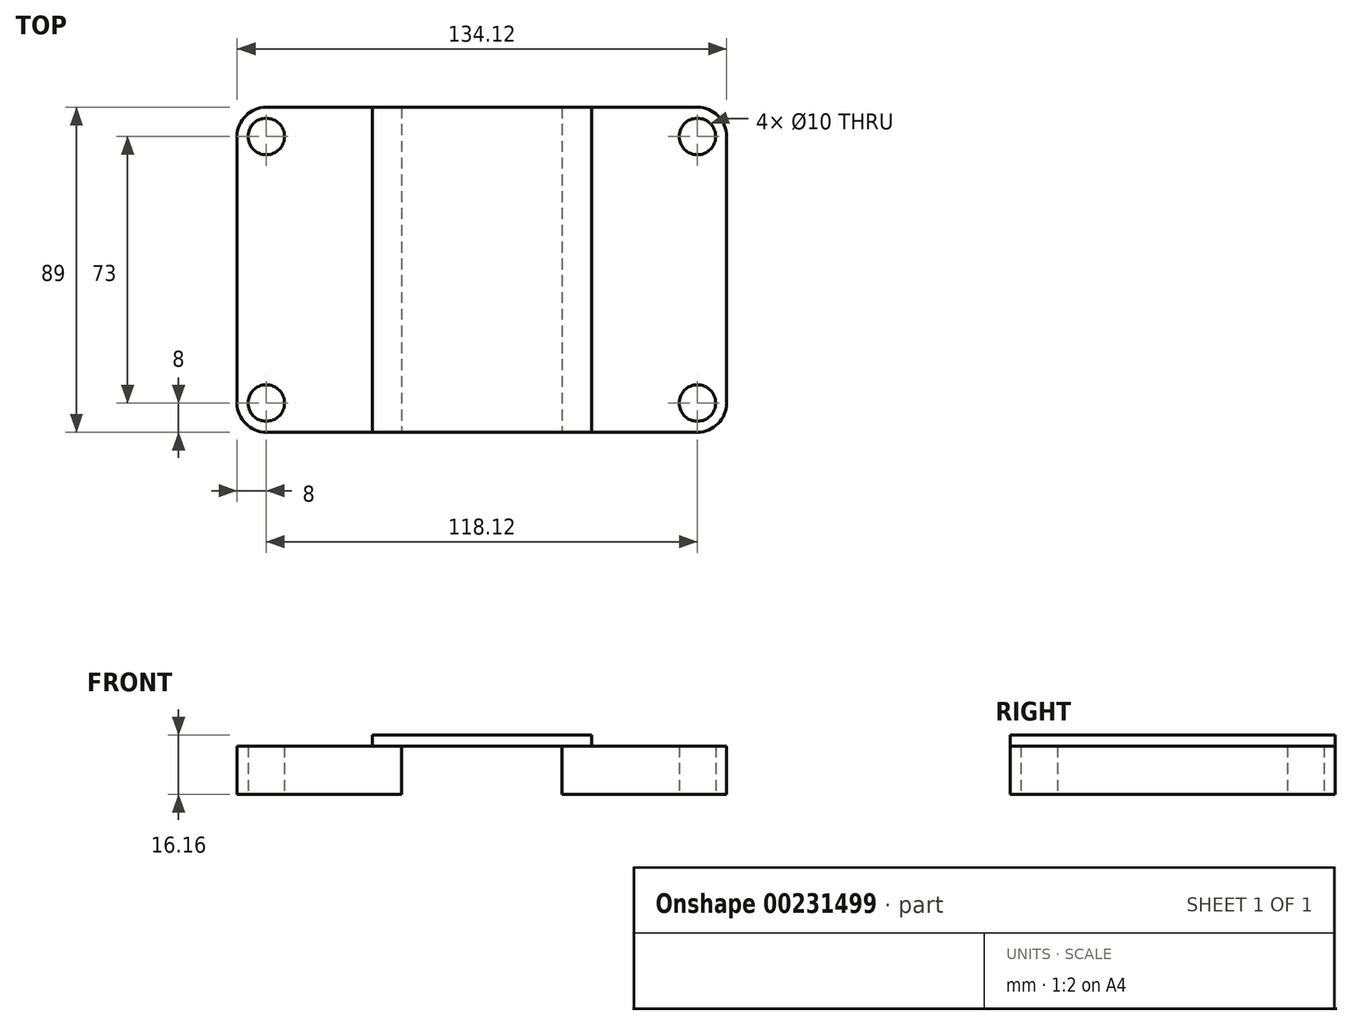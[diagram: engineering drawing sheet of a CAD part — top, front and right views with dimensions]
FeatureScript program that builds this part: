
annotation { "Feature Type Name" : "Feature", "Feature Type Description" : "" }
export const myFeature = defineFeature(function(context is Context, id is Id, definition is map)
    precondition{}
    {
        {
            var Q0;
            Q0=qCreatedBy(makeId("Top.planeOp"),FACE);
            var sketch = newSketch(context, id + "F0", { "sketchPlane" : qUnion([Q0])});
            skLineSegment(sketch, "E0.bottom", {"start": v(59.06, -44.5) * mm, "end": v(-59.06, -44.5) * mm});
            skLineSegment(sketch, "E0.top", {"start": v(67.06, 44.5) * mm, "end": v(-67.06, 44.5) * mm});
            skLineSegment(sketch, "E0.left", {"start": v(67.06, -36.5) * mm, "end": v(67.06, 36.5) * mm});
            skLineSegment(sketch, "E0.right", {"start": v(-67.06, -36.5) * mm, "end": v(-67.06, 36.5) * mm});
            skPoint(sketch, "E0.middle", {"position": v(0, 0) * mm});
            skLineSegment(sketch, "E1", {"start": v(-59.06, 44.5) * mm, "end": v(-21.96, 44.5) * mm});
            skLineSegment(sketch, "E2", {"start": v(-21.96, 44.5) * mm, "end": v(-21.96, -44.5) * mm});
            skLineSegment(sketch, "E3", {"start": v(-21.96, 44.5) * mm, "end": v(21.94, 44.5) * mm});
            skLineSegment(sketch, "E4", {"start": v(21.94, 44.5) * mm, "end": v(59.06, 44.5) * mm});
            skLineSegment(sketch, "E5", {"start": v(21.94, 44.5) * mm, "end": v(21.94, -44.5) * mm});
            skPoint(sketch, "E6.visualSharp", {"position": v(-67.06, 44.5) * mm});
            skArc(sketch, "E6.filletArc", {"start": v(-59.06, 44.5) * mm, "mid": v(-64.72, 42.16) * mm, "end": v(-67.06, 36.5) * mm});
            skPoint(sketch, "E7.visualSharp", {"position": v(67.06, 44.5) * mm});
            skArc(sketch, "E7.filletArc", {"start": v(67.06, 36.5) * mm, "mid": v(64.72, 42.16) * mm, "end": v(59.06, 44.5) * mm});
            skPoint(sketch, "E8.visualSharp", {"position": v(67.06, -44.5) * mm});
            skArc(sketch, "E8.filletArc", {"start": v(59.06, -44.5) * mm, "mid": v(64.72, -42.16) * mm, "end": v(67.06, -36.5) * mm});
            skPoint(sketch, "E9.visualSharp", {"position": v(-67.06, -44.5) * mm});
            skArc(sketch, "E9.filletArc", {"start": v(-67.06, -36.5) * mm, "mid": v(-64.72, -42.16) * mm, "end": v(-59.06, -44.5) * mm});
            skCircle(sketch, "E10", {"center": v(-59.06, 36.5) * mm, "radius": 5 * mm});
            skCircle(sketch, "E11", {"center": v(-59.06, -36.5) * mm, "radius": 5 * mm});
            skCircle(sketch, "E12", {"center": v(59.06, 36.5) * mm, "radius": 5 * mm});
            skCircle(sketch, "E13", {"center": v(59.06, -36.5) * mm, "radius": 5 * mm});
            skSolve(sketch);
        }
        {
            var Q0;
            {var subQ0=sQuery(id+"F0.wireOp",EDGE,"E0.right");Q0=makeQuery(id+"F0.imprint","IMPRINT",FACE,{"disambiguationData":[TD([[makeQuery(id+"F0.imprint","IMPRINT",EDGE,{"derivedFrom":subQ0}),-1.0]])]});}
            var Q1;
            {var subQ0=sQuery(id+"F0.wireOp",EDGE,"E0.left");Q1=makeQuery(id+"F0.imprint","IMPRINT",FACE,{"disambiguationData":[TD([[makeQuery(id+"F0.imprint","IMPRINT",EDGE,{"derivedFrom":subQ0}),1.0]])]});}
            extrude(context, id + "F1", {"entities" : qUnion([Q0, Q1]), "depth" : 13.16 * mm});
        }
        {
            var Q0;
            Q0=makeQuery(id+"F1.opExtrude","CAP_FACE",FACE,{"disambiguationData":[OSD([sQuery(id+"F0.wireOp",EDGE,"E0.bottom"),sQuery(id+"F0.wireOp",EDGE,"E0.right"),sQuery(id+"F0.wireOp",EDGE,"E1"),sQuery(id+"F0.wireOp",EDGE,"E2")])],"isStart":false});
            var sketch = newSketch(context, id + "F2", { "sketchPlane" : qUnion([Q0])});
            skLineSegment(sketch, "E14", {"start": v(0, 44.5) * mm, "end": v(-30.04, 44.5) * mm});
            skLineSegment(sketch, "E15", {"start": v(0, 44.5) * mm, "end": v(30.04, 44.5) * mm});
            skLineSegment(sketch, "E16", {"start": v(-30.04, 44.5) * mm, "end": v(-30.04, -44.5) * mm});
            skLineSegment(sketch, "E17", {"start": v(-30.04, -44.5) * mm, "end": v(30.04, -44.5) * mm});
            skLineSegment(sketch, "E18", {"start": v(30.04, -44.5) * mm, "end": v(30.04, 44.5) * mm});
            skSolve(sketch);
        }
        {
            var Q0;
            {var subQ3=sQuery(id+"F2.wireOp",EDGE,"E15");Q0=makeQuery(id+"F2.imprint","IMPRINT",FACE,{"disambiguationData":[TD([[makeQuery(id+"F2.imprint","IMPRINT",EDGE,{"derivedFrom":subQ3}),-1.0]])]});}
            var Q1;
            {var subQ3=sQuery(id+"F2.wireOp",EDGE,"E16");Q1=makeQuery(id+"F2.imprint","IMPRINT",FACE,{"disambiguationData":[TD([[makeQuery(id+"F2.imprint","IMPRINT",EDGE,{"derivedFrom":subQ3}),1.0]])]});}
            extrude(context, id + "F3", {"entities" : qUnion([Q0, Q1]), "depth" : 3 * mm});
        }
        {
            var Q0;
            Q0=makeQuery(id+"F0.imprint","IMPRINT",FACE,{"disambiguationData":[TD([[makeQuery(id+"F0.imprint","IMPRINT",EDGE,{"derivedFrom":sQuery(id+"F0.wireOp",EDGE,"E13")}),1.0]])]});
            var Q1;
            Q1=makeQuery(id+"F0.imprint","IMPRINT",FACE,{"disambiguationData":[TD([[makeQuery(id+"F0.imprint","IMPRINT",EDGE,{"derivedFrom":sQuery(id+"F0.wireOp",EDGE,"E11")}),1.0]])]});
            var Q2;
            Q2=makeQuery(id+"F0.imprint","IMPRINT",FACE,{"disambiguationData":[TD([[makeQuery(id+"F0.imprint","IMPRINT",EDGE,{"derivedFrom":sQuery(id+"F0.wireOp",EDGE,"E10")}),1.0]])]});
            var Q3;
            Q3=makeQuery(id+"F0.imprint","IMPRINT",FACE,{"disambiguationData":[TD([[makeQuery(id+"F0.imprint","IMPRINT",EDGE,{"derivedFrom":sQuery(id+"F0.wireOp",EDGE,"E12")}),1.0]])]});
            extrude(context, id + "F4", {"entities" : qUnion([Q0, Q1, Q2, Q3]), "operationType" : NewBodyOperationType.REMOVE, "endBound" : BoundingType.THROUGH_ALL, "oppositeDirection" : true, "depth" : 25.4 * mm});
        }
    });
